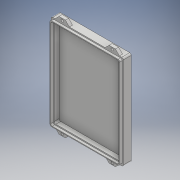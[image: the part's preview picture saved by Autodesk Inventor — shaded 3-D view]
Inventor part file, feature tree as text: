
AUTODESK INVENTOR PART (.ipt)
format: ipt  version: 2017 (Build 210142000, 142)  size: 202,752 bytes
history: native  units: mm
features: sketch x4, extrude x4, fillet x2
ambient origin geometry x8: Origin, YZ Plane, XZ Plane, XY Plane, X Axis, Y Axis, Z Axis, Center Point
bodies: Solid1 (feature_tree)
feature tree (10):
  sketch  "Sketch1"  dims[d0=10.0mm d1=0.0mm d2=4.0mm]
  extrude  "Extrusion1"  Depth=4.0mm
  extrude  "Extrusion2"  Depth=4.0mm
  fillet  "Fillet1"  Radius=4.0mm
  extrude  "Extrusion3"  Depth=2.0mm
  extrude  "Extrusion4"  Depth=1.5mm
  fillet  "Fillet2"  Radius=1.5mm
  sketch  "Sketch4"  dims[d3=4.0mm d4=4.0mm d5=4.0mm]
  sketch  "Sketch5"  dims[d6=6.0mm d7=0.0mm d8=2.0mm]
  sketch  "Sketch6"  dims[d9=6.0mm d10=0.0mm d11=1.5mm d12=1.5mm d13=1.5mm d14=1.5mm d15=1.0mm d16=1.0mm d17=1.0mm d18=1.0mm d19=3.0mm d20=0.0mm d21=2.0mm]
